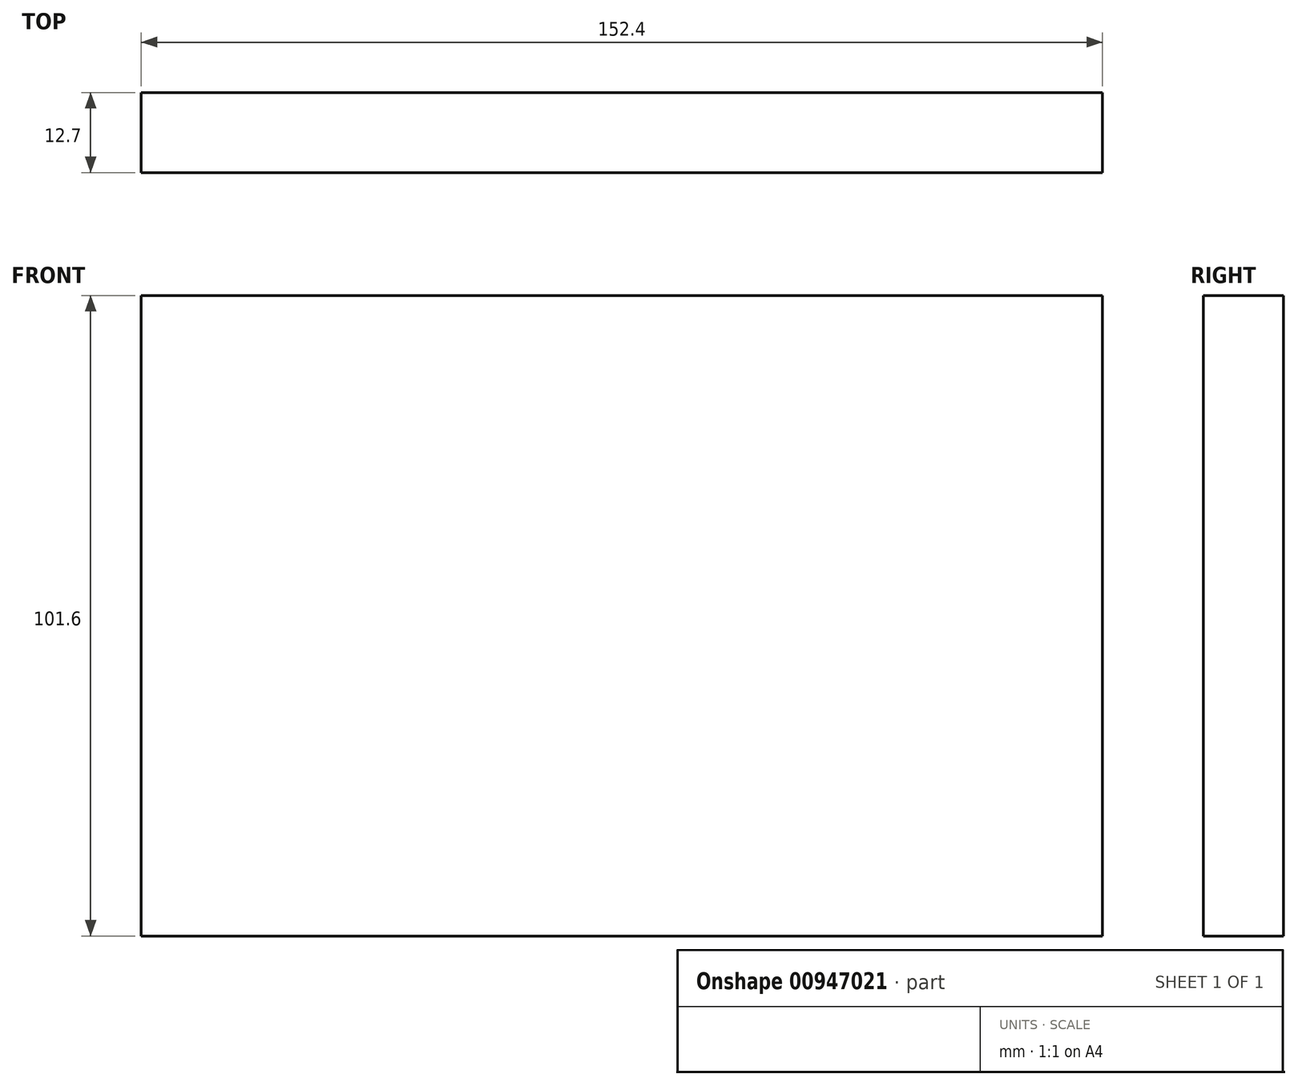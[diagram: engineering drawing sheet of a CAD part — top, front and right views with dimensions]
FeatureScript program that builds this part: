
annotation { "Feature Type Name" : "Feature", "Feature Type Description" : "" }
export const myFeature = defineFeature(function(context is Context, id is Id, definition is map)
    precondition{}
    {
        {
            var Q0;
            Q0=qCreatedBy(makeId("Front.planeOp"),FACE);
            var sketch = newSketch(context, id + "F0", { "sketchPlane" : qUnion([Q0])});
            skLineSegment(sketch, "E0.bottom", {"start": v(0, 0) * mm, "end": v(152.4, 0) * mm});
            skLineSegment(sketch, "E0.top", {"start": v(0, 101.6) * mm, "end": v(152.4, 101.6) * mm});
            skLineSegment(sketch, "E0.left", {"start": v(0, 0) * mm, "end": v(0, 101.6) * mm});
            skLineSegment(sketch, "E0.right", {"start": v(152.4, 0) * mm, "end": v(152.4, 101.6) * mm});
            skSolve(sketch);
        }
        {
            var Q0;
            Q0 = qSketchRegion(id + "F0", true);
            extrude(context, id + "F1", {"entities" : qUnion([Q0]), "depth" : 12.7 * mm, "offsetDistance" : 25.4 * mm});
        }
    });
